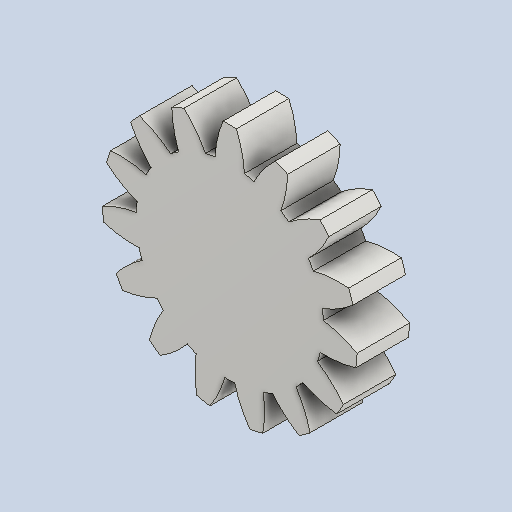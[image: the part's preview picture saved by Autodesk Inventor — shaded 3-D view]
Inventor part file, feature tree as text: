
AUTODESK INVENTOR PART (.ipt)
format: ipt  version: 2025.2 (Build 292293000, 293)  size: 219,136 bytes
history: native  units: mm (DEFAULTED — no unit token found)
features: plane x3, other x3, extrude x1, sketch x1
ambient origin geometry x8: Origin, YZ Plane, XZ Plane, XY Plane, X Axis, Y Axis, Z Axis, Center Point
bodies: Solid1 (feature_tree)
feature tree (8):
  extrude  "Extrusion1"  Depth=7.0mm TaperAngle=0.0deg
  plane  "Work Plane2"
  plane  "Work Plane8"
  plane  "Work Plane9"
  other  "Spur Gear"
  sketch  "Sketch1"  dims[d0=34.0mm d1=7.0mm d2=0.0mm d3=30.0mm d4=10.0mm d5=0.0mm d16=60.0mm d17=0.0mm d34=2.094395mm d39=0.0mm d41=0.0mm d43=60.0mm d46=60.0mm d47=0.0mm d48=0.0mm]
  other  "Srf1"
  other  "Pitch Diameter"
